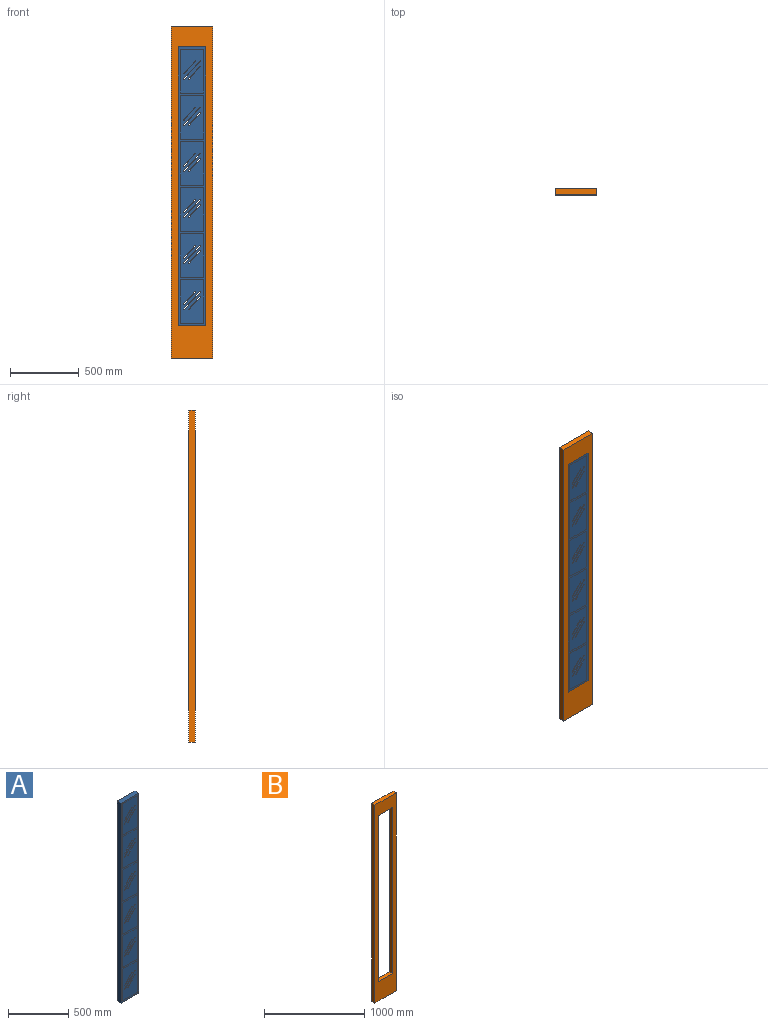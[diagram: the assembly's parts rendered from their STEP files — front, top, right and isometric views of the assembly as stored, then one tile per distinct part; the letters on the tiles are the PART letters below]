
ASSEMBLY  parts=2 mates=1
PART A: 138 faces, bbox 203.2x44.5x2032 mm
  f0: plane 171.45x0.64mm, normal (0,0,-1), area 108.9mm2, adj f1,f3,f53,f137
  f1: plane 320.15x0.64mm, normal (-1,0,0), area 203.3mm2, adj f0,f2,f53,f137
  f2: plane 171.45x0.64mm, normal (0,0,1), area 108.9mm2, adj f1,f3,f53,f137
  f3: plane 320.15x0.64mm, normal (1,0,0), area 203.3mm2, adj f0,f2,f53,f137
  f4: plane 320.15x0.64mm, normal (1,0,0), area 203.3mm2, adj f5,f7,f53,f123
  f5: plane 171.45x0.64mm, normal (0,0,-1), area 108.9mm2, adj f4,f6,f53,f123
  f6: plane 320.15x0.64mm, normal (-1,0,0), area 203.3mm2, adj f5,f7,f53,f123
  f7: plane 171.45x0.64mm, normal (0,0,1), area 108.9mm2, adj f4,f6,f53,f123
  f8: plane 171.45x0.64mm, normal (0,0,-1), area 108.9mm2, adj f9,f11,f53,f109
  f9: plane 320.15x0.64mm, normal (-1,0,0), area 203.3mm2, adj f8,f10,f53,f109
  f10: plane 171.45x0.64mm, normal (0,0,1), area 108.9mm2, adj f9,f11,f53,f109
  f11: plane 320.15x0.64mm, normal (1,0,0), area 203.3mm2, adj f8,f10,f53,f109
  f12: plane 171.45x0.64mm, normal (0,0,-1), area 108.9mm2, adj f13,f15,f53,f95
  f13: plane 320.15x0.64mm, normal (-1,0,0), area 203.3mm2, adj f12,f14,f53,f95
  f14: plane 171.45x0.64mm, normal (0,0,1), area 108.9mm2, adj f13,f15,f53,f95
  f15: plane 320.15x0.64mm, normal (1,0,0), area 203.3mm2, adj f12,f14,f53,f95
  f16: plane 171.45x0.64mm, normal (0,0,-1), area 108.9mm2, adj f17,f19,f53,f81
  f17: plane 320.15x0.64mm, normal (-1,0,0), area 203.3mm2, adj f16,f18,f53,f81
  f18: plane 171.45x0.64mm, normal (0,0,1), area 108.9mm2, adj f17,f19,f53,f81
  f19: plane 320.15x0.64mm, normal (1,0,0), area 203.3mm2, adj f16,f18,f53,f81
  f20: plane 171.45x0.64mm, normal (0,0,-1), area 108.9mm2, adj f21,f23,f53,f67
  f21: plane 320.15x0.64mm, normal (-1,0,0), area 203.3mm2, adj f20,f22,f53,f67
  f22: plane 171.45x0.64mm, normal (0,0,1), area 108.9mm2, adj f21,f23,f53,f67
  f23: plane 320.15x0.64mm, normal (1,0,0), area 203.3mm2, adj f20,f22,f53,f67
  f24: plane 320.15x0.64mm, normal (1,0,0), area 203.3mm2, adj f25,f51,f52,f122
  f25: plane 171.45x0.64mm, normal (0,0,-1), area 108.9mm2, adj f24,f26,f52,f122
  f26: plane 320.15x0.64mm, normal (-1,0,0), area 203.3mm2, adj f25,f51,f52,f122
  f27: plane 203.2x44.45mm, normal (0,0,1), area 9032.2mm2, adj f28,f45,f52,f53
  f28: plane 2032x44.45mm, normal (-1,0,0), area 90322.4mm2, adj f27,f29,f52,f53
  f29: plane 203.2x44.45mm, normal (0,0,-1), area 9032.2mm2, adj f28,f45,f52,f53
  f30: plane 171.45x0.64mm, normal (0,0,-1), area 108.9mm2, adj f31,f46,f52,f108
  f31: plane 320.15x0.64mm, normal (-1,0,0), area 203.3mm2, adj f30,f32,f52,f108
  f32: plane 171.45x0.64mm, normal (0,0,1), area 108.9mm2, adj f31,f46,f52,f108
  f33: plane 171.45x0.64mm, normal (0,0,-1), area 108.9mm2, adj f34,f47,f52,f94
  f34: plane 320.15x0.64mm, normal (-1,0,0), area 203.3mm2, adj f33,f35,f52,f94
  f35: plane 171.45x0.64mm, normal (0,0,1), area 108.9mm2, adj f34,f47,f52,f94
  f36: plane 171.45x0.64mm, normal (0,0,-1), area 108.9mm2, adj f37,f48,f52,f80
  f37: plane 320.15x0.64mm, normal (-1,0,0), area 203.3mm2, adj f36,f38,f52,f80
  f38: plane 171.45x0.64mm, normal (0,0,1), area 108.9mm2, adj f37,f48,f52,f80
  f39: plane 171.45x0.64mm, normal (0,0,-1), area 108.9mm2, adj f40,f49,f52,f66
  f40: plane 320.15x0.64mm, normal (-1,0,0), area 203.3mm2, adj f39,f41,f52,f66
  f41: plane 171.45x0.64mm, normal (0,0,1), area 108.9mm2, adj f40,f49,f52,f66
  f42: plane 171.45x0.64mm, normal (0,0,-1), area 108.9mm2, adj f43,f50,f52,f136
  f43: plane 320.15x0.64mm, normal (-1,0,0), area 203.3mm2, adj f42,f44,f52,f136
  f44: plane 171.45x0.64mm, normal (0,0,1), area 108.9mm2, adj f43,f50,f52,f136
  f45: plane 2032x44.45mm, normal (1,0,0), area 90322.4mm2, adj f27,f29,f52,f53
  f46: plane 320.15x0.64mm, normal (1,0,0), area 203.3mm2, adj f30,f32,f52,f108
  f47: plane 320.15x0.64mm, normal (1,0,0), area 203.3mm2, adj f33,f35,f52,f94
  f48: plane 320.15x0.64mm, normal (1,0,0), area 203.3mm2, adj f36,f38,f52,f80
  f49: plane 320.15x0.64mm, normal (1,0,0), area 203.3mm2, adj f39,f41,f52,f66
  f50: plane 320.15x0.64mm, normal (1,0,0), area 203.3mm2, adj f42,f44,f52,f136
  f51: plane 171.45x0.64mm, normal (0,0,1), area 108.9mm2, adj f24,f26,f52,f122
  f52: plane 2032x203.2mm, normal (0,-1,0), area 83568.4mm2, adj f24,f25,f26,f27,f28,f29,f30,f31
  f53: plane 2032x203.2mm, normal (0,1,0), area 83568.4mm2, adj f0,f1,f2,f3,f4,f5,f6,f7
  f54: cylinder r=3.17mm len=43.18mm, axis (0,1,0), area 430.7mm2, adj f55,f65,f66,f67
  f55: plane 88.11x82.76mm, normal (-0.73,0,0.68), area 5219.7mm2, adj f54,f56,f66,f67
  f56: cylinder r=3.17mm len=43.18mm, axis (0,1,0), area 430.7mm2, adj f55,f65,f66,f67
  f57: cylinder r=3.17mm len=43.18mm, axis (0,1,0), area 430.7mm2, adj f58,f63,f66,f67
  f58: plane 88.11x82.76mm, normal (-0.73,0,0.68), area 5219.7mm2, adj f57,f59,f66,f67
  f59: cylinder r=3.17mm len=43.18mm, axis (0,1,0), area 430.7mm2, adj f58,f63,f66,f67
  f60: plane 126.21x118.54mm, normal (0.73,0,-0.68), area 7476.7mm2, adj f61,f64,f66,f67
  f61: cylinder r=3.17mm len=43.18mm, axis (0,1,0), area 430.7mm2, adj f60,f62,f66,f67
  f62: plane 126.21x118.54mm, normal (-0.73,0,0.68), area 7476.7mm2, adj f61,f64,f66,f67
  f63: plane 88.11x82.76mm, normal (0.73,0,-0.68), area 5219.7mm2, adj f57,f59,f66,f67
  f64: cylinder r=3.17mm len=43.18mm, axis (0,1,0), area 430.7mm2, adj f60,f62,f66,f67
  f65: plane 88.11x82.76mm, normal (0.73,0,-0.68), area 5219.7mm2, adj f54,f56,f66,f67
  f66: plane 320.15x171.45mm, normal (0,-1,0), area 52159.3mm2, adj f39,f40,f41,f49,f54,f55,f56,f57
  f67: plane 320.15x171.45mm, normal (0,1,0), area 52159.3mm2, adj f20,f21,f22,f23,f54,f55,f56,f57
  f68: cylinder r=3.17mm len=43.18mm, axis (0,1,0), area 430.7mm2, adj f69,f79,f80,f81
  f69: plane 88.11x82.76mm, normal (-0.73,0,0.68), area 5219.7mm2, adj f68,f70,f80,f81
  f70: cylinder r=3.17mm len=43.18mm, axis (0,1,0), area 430.7mm2, adj f69,f79,f80,f81
  f71: cylinder r=3.17mm len=43.18mm, axis (0,1,0), area 430.7mm2, adj f72,f77,f80,f81
  f72: plane 88.11x82.76mm, normal (-0.73,0,0.68), area 5219.7mm2, adj f71,f73,f80,f81
  f73: cylinder r=3.17mm len=43.18mm, axis (0,1,0), area 430.7mm2, adj f72,f77,f80,f81
  f74: plane 126.21x118.54mm, normal (0.73,0,-0.68), area 7476.7mm2, adj f75,f78,f80,f81
  f75: cylinder r=3.17mm len=43.18mm, axis (0,1,0), area 430.7mm2, adj f74,f76,f80,f81
  f76: plane 126.21x118.54mm, normal (-0.73,0,0.68), area 7476.7mm2, adj f75,f78,f80,f81
  f77: plane 88.11x82.76mm, normal (0.73,0,-0.68), area 5219.7mm2, adj f71,f73,f80,f81
  f78: cylinder r=3.17mm len=43.18mm, axis (0,1,0), area 430.7mm2, adj f74,f76,f80,f81
  f79: plane 88.11x82.76mm, normal (0.73,0,-0.68), area 5219.7mm2, adj f68,f70,f80,f81
  f80: plane 320.15x171.45mm, normal (0,-1,0), area 52159.3mm2, adj f36,f37,f38,f48,f68,f69,f70,f71
  f81: plane 320.15x171.45mm, normal (0,1,0), area 52159.3mm2, adj f16,f17,f18,f19,f68,f69,f70,f71
  f82: cylinder r=3.17mm len=43.18mm, axis (0,1,0), area 430.7mm2, adj f83,f93,f94,f95
  f83: plane 88.11x82.76mm, normal (-0.73,0,0.68), area 5219.7mm2, adj f82,f84,f94,f95
  f84: cylinder r=3.17mm len=43.18mm, axis (0,1,0), area 430.7mm2, adj f83,f93,f94,f95
  f85: cylinder r=3.17mm len=43.18mm, axis (0,1,0), area 430.7mm2, adj f86,f91,f94,f95
  f86: plane 88.11x82.76mm, normal (-0.73,0,0.68), area 5219.7mm2, adj f85,f87,f94,f95
  f87: cylinder r=3.17mm len=43.18mm, axis (0,1,0), area 430.7mm2, adj f86,f91,f94,f95
  f88: plane 126.21x118.54mm, normal (0.73,0,-0.68), area 7476.7mm2, adj f89,f92,f94,f95
  f89: cylinder r=3.17mm len=43.18mm, axis (0,1,0), area 430.7mm2, adj f88,f90,f94,f95
  f90: plane 126.21x118.54mm, normal (-0.73,0,0.68), area 7476.7mm2, adj f89,f92,f94,f95
  f91: plane 88.11x82.76mm, normal (0.73,0,-0.68), area 5219.7mm2, adj f85,f87,f94,f95
  f92: cylinder r=3.17mm len=43.18mm, axis (0,1,0), area 430.7mm2, adj f88,f90,f94,f95
  f93: plane 88.11x82.76mm, normal (0.73,0,-0.68), area 5219.7mm2, adj f82,f84,f94,f95
  f94: plane 320.15x171.45mm, normal (0,-1,0), area 52159.3mm2, adj f33,f34,f35,f47,f82,f83,f84,f85
  f95: plane 320.15x171.45mm, normal (0,1,0), area 52159.3mm2, adj f12,f13,f14,f15,f82,f83,f84,f85
  f96: cylinder r=3.17mm len=43.18mm, axis (0,1,0), area 430.7mm2, adj f97,f107,f108,f109
  f97: plane 88.11x82.76mm, normal (-0.73,0,0.68), area 5219.7mm2, adj f96,f98,f108,f109
  f98: cylinder r=3.17mm len=43.18mm, axis (0,1,0), area 430.7mm2, adj f97,f107,f108,f109
  f99: cylinder r=3.17mm len=43.18mm, axis (0,1,0), area 430.7mm2, adj f100,f105,f108,f109
  f100: plane 88.11x82.76mm, normal (-0.73,0,0.68), area 5219.7mm2, adj f99,f101,f108,f109
  f101: cylinder r=3.17mm len=43.18mm, axis (0,1,0), area 430.7mm2, adj f100,f105,f108,f109
  f102: plane 126.21x118.54mm, normal (0.73,0,-0.68), area 7476.7mm2, adj f103,f106,f108,f109
  f103: cylinder r=3.17mm len=43.18mm, axis (0,1,0), area 430.7mm2, adj f102,f104,f108,f109
  f104: plane 126.21x118.54mm, normal (-0.73,0,0.68), area 7476.7mm2, adj f103,f106,f108,f109
  f105: plane 88.11x82.76mm, normal (0.73,0,-0.68), area 5219.7mm2, adj f99,f101,f108,f109
  f106: cylinder r=3.17mm len=43.18mm, axis (0,1,0), area 430.7mm2, adj f102,f104,f108,f109
  f107: plane 88.11x82.76mm, normal (0.73,0,-0.68), area 5219.7mm2, adj f96,f98,f108,f109
  f108: plane 320.15x171.45mm, normal (0,-1,0), area 52159.3mm2, adj f30,f31,f32,f46,f96,f97,f98,f99
  f109: plane 320.15x171.45mm, normal (0,1,0), area 52159.3mm2, adj f8,f9,f10,f11,f96,f97,f98,f99
  f110: plane 88.11x82.76mm, normal (-0.73,0,0.68), area 5219.7mm2, adj f111,f121,f122,f123
  f111: cylinder r=3.17mm len=43.18mm, axis (0,1,0), area 430.7mm2, adj f110,f112,f122,f123
  f112: plane 88.11x82.76mm, normal (0.73,0,-0.68), area 5219.7mm2, adj f111,f121,f122,f123
  f113: plane 126.21x118.54mm, normal (0.73,0,-0.68), area 7476.7mm2, adj f114,f119,f122,f123
  f114: cylinder r=3.17mm len=43.18mm, axis (0,1,0), area 430.7mm2, adj f113,f115,f122,f123
  f115: plane 126.21x118.54mm, normal (-0.73,0,0.68), area 7476.7mm2, adj f114,f119,f122,f123
  f116: plane 88.11x82.76mm, normal (-0.73,0,0.68), area 5219.7mm2, adj f117,f120,f122,f123
  f117: cylinder r=3.17mm len=43.18mm, axis (0,1,0), area 430.7mm2, adj f116,f118,f122,f123
  f118: plane 88.11x82.76mm, normal (0.73,0,-0.68), area 5219.7mm2, adj f117,f120,f122,f123
  f119: cylinder r=3.17mm len=43.18mm, axis (0,1,0), area 430.7mm2, adj f113,f115,f122,f123
  f120: cylinder r=3.17mm len=43.18mm, axis (0,1,0), area 430.7mm2, adj f116,f118,f122,f123
  f121: cylinder r=3.17mm len=43.18mm, axis (0,1,0), area 430.7mm2, adj f110,f112,f122,f123
  f122: plane 320.15x171.45mm, normal (0,-1,0), area 52159.3mm2, adj f24,f25,f26,f51,f110,f111,f112,f113
  f123: plane 320.15x171.45mm, normal (0,1,0), area 52159.3mm2, adj f4,f5,f6,f7,f110,f111,f112,f113
  f124: cylinder r=3.17mm len=43.18mm, axis (0,1,0), area 430.7mm2, adj f125,f135,f136,f137
  f125: plane 88.11x82.76mm, normal (-0.73,0,0.68), area 5219.7mm2, adj f124,f126,f136,f137
  f126: cylinder r=3.17mm len=43.18mm, axis (0,1,0), area 430.7mm2, adj f125,f135,f136,f137
  f127: cylinder r=3.17mm len=43.18mm, axis (0,1,0), area 430.7mm2, adj f128,f133,f136,f137
  f128: plane 88.11x82.76mm, normal (-0.73,0,0.68), area 5219.7mm2, adj f127,f129,f136,f137
  f129: cylinder r=3.17mm len=43.18mm, axis (0,1,0), area 430.7mm2, adj f128,f133,f136,f137
  f130: plane 126.21x118.54mm, normal (0.73,0,-0.68), area 7476.7mm2, adj f131,f134,f136,f137
  f131: cylinder r=3.17mm len=43.18mm, axis (0,1,0), area 430.7mm2, adj f130,f132,f136,f137
  f132: plane 126.21x118.54mm, normal (-0.73,0,0.68), area 7476.7mm2, adj f131,f134,f136,f137
  f133: plane 88.11x82.76mm, normal (0.73,0,-0.68), area 5219.7mm2, adj f127,f129,f136,f137
  f134: cylinder r=3.17mm len=43.18mm, axis (0,1,0), area 430.7mm2, adj f130,f132,f136,f137
  f135: plane 88.11x82.76mm, normal (0.73,0,-0.68), area 5219.7mm2, adj f124,f126,f136,f137
  f136: plane 320.15x171.45mm, normal (0,-1,0), area 52159.3mm2, adj f42,f43,f44,f50,f124,f125,f126,f127
  f137: plane 320.15x171.45mm, normal (0,1,0), area 52159.3mm2, adj f0,f1,f2,f3,f124,f125,f126,f127
PART B: 10 faces, bbox 301.6x44.5x2419.4 mm
  f0: plane 301.63x44.45mm, normal (0,0,1), area 13407.2mm2, adj f1,f7,f8,f9
  f1: plane 2419.35x44.45mm, normal (-1,0,0), area 107540.1mm2, adj f0,f2,f8,f9
  f2: plane 301.63x44.45mm, normal (0,0,-1), area 13407.2mm2, adj f1,f7,f8,f9
  f3: plane 203.2x44.45mm, normal (0,0,1), area 9032.2mm2, adj f4,f6,f8,f9
  f4: plane 2032x44.45mm, normal (1,0,0), area 90322.4mm2, adj f3,f5,f8,f9
  f5: plane 203.2x44.45mm, normal (0,0,-1), area 9032.2mm2, adj f4,f6,f8,f9
  f6: plane 2032x44.45mm, normal (-1,0,0), area 90322.4mm2, adj f3,f5,f8,f9
  f7: plane 2419.35x44.45mm, normal (1,0,0), area 107540.1mm2, adj f0,f2,f8,f9
  f8: plane 2419.35x301.63mm, normal (0,-1,0), area 316834mm2, adj f0,f1,f2,f3,f4,f5,f6,f7
  f9: plane 2419.35x301.63mm, normal (0,1,0), area 316834mm2, adj f0,f1,f2,f3,f4,f5,f6,f7
PLACE A t=(49.21,0,234.95)mm
PLACE B at identity
MATE fastened A.f27 <-> B.f5  axis (0,0,1) through (150.81,0,2266.95)mm
